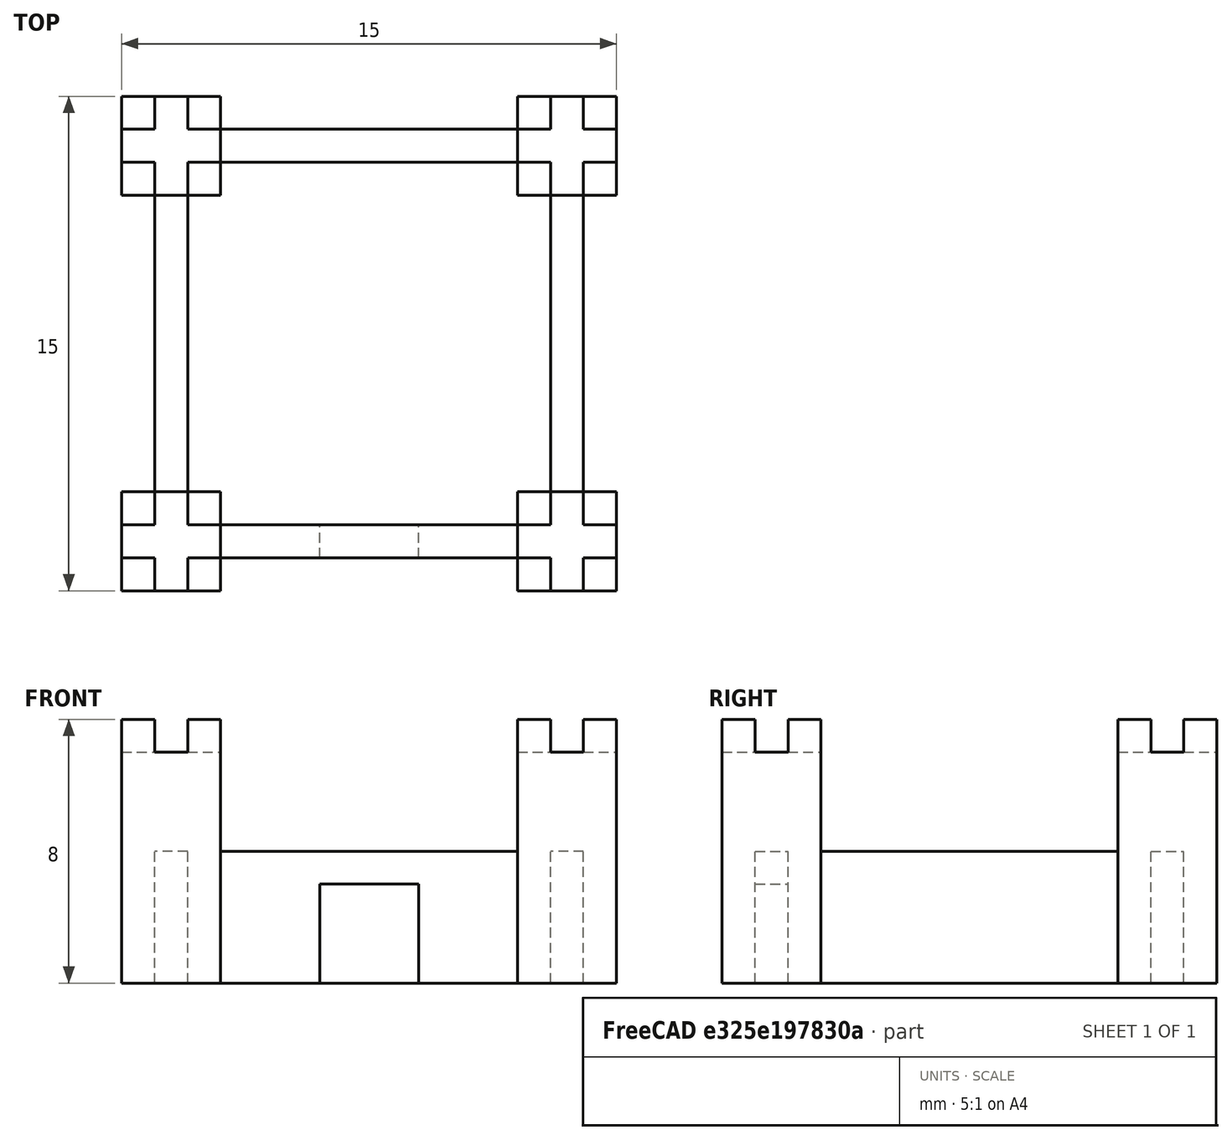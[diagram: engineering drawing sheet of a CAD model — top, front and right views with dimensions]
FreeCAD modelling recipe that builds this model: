
FCSTD DOCUMENT  (FreeCAD 0.20R29177 +233 (Git))
Label: Castillo
License: Creative Commons Attribution-ShareAlike
LicenseURL: http://creativecommons.org/licenses/by-sa/4.0/
objects: Part::Box×25, Part::MultiFuse×23, Part::Cut×1
note: 49 computed .brp shape members not serialized (recipe doc carries the construction recipe); baked Part::Feature solids carry a one-line shape summary decoded from their .brp

FEATURE [Part::Box] Box  label="Cubo"
  AttacherType = Attacher::AttachEngine3D
  Height = 4
  Length = 9
  Width = 1
FEATURE [Part::Box] Box001  label="Cubo001"
  AttacherType = Attacher::AttachEngine3D
  Height = 7
  Length = 3
  Placement = pos=(-3,-1,0) rot=(0,0,1;0rad)
  Width = 3
FEATURE [Part::Box] Box003  label="Cubo003"
  AttacherType = Attacher::AttachEngine3D
  Height = 4
  Length = 9
  Placement = pos=(-1,2,0) rot=(0,0,1;1.5708rad)
  Width = 1
FEATURE [Part::Box] Box004  label="Cubo004"
  AttacherType = Attacher::AttachEngine3D
  Height = 4
  Length = 9
  Placement = pos=(11,2,0) rot=(0,0,1;1.5708rad)
  Width = 1
FEATURE [Part::Box] Box005  label="Cubo005"
  AttacherType = Attacher::AttachEngine3D
  Height = 1
  Length = 1
  Placement = pos=(-1,1,7) rot=(0,0,1;0rad)
  Width = 1
FEATURE [Part::Box] Box006  label="Cubo006"
  AttacherType = Attacher::AttachEngine3D
  Height = 1
  Length = 1
  Placement = pos=(-1,-1,7) rot=(0,0,1;0rad)
  Width = 1
FEATURE [Part::Box] Box007  label="Cubo007"
  AttacherType = Attacher::AttachEngine3D
  Height = 1
  Length = 1
  Placement = pos=(-3,-1,7) rot=(0,0,1;0rad)
  Width = 1
FEATURE [Part::Box] Box008  label="Cubo008"
  AttacherType = Attacher::AttachEngine3D
  Height = 1
  Length = 1
  Placement = pos=(-3,1,7) rot=(0,0,1;0rad)
  Width = 1
FEATURE [Part::MultiFuse] Fusion
  Refine = true
  Shapes = -> [Box001,Box007]
FEATURE [Part::MultiFuse] Fusion001
  Refine = true
  Shapes = -> [Fusion,Box008]
FEATURE [Part::MultiFuse] Fusion002
  Refine = true
  Shapes = -> [Fusion001,Box006]
FEATURE [Part::MultiFuse] Fusion003
  Refine = true
  Shapes = -> [Fusion002,Box005]
FEATURE [Part::Box] Box009  label="Cubo009"
  AttacherType = Attacher::AttachEngine3D
  Height = 7
  Length = 3
  Placement = pos=(-3,-1,0) rot=(0,0,1;0rad)
  Width = 3
FEATURE [Part::Box] Box010  label="Cubo010"
  AttacherType = Attacher::AttachEngine3D
  Height = 1
  Length = 1
  Placement = pos=(-1,1,7) rot=(0,0,1;0rad)
  Width = 1
FEATURE [Part::Box] Box011  label="Cubo011"
  AttacherType = Attacher::AttachEngine3D
  Height = 1
  Length = 1
  Placement = pos=(-1,-1,7) rot=(0,0,1;0rad)
  Width = 1
FEATURE [Part::Box] Box012  label="Cubo012"
  AttacherType = Attacher::AttachEngine3D
  Height = 1
  Length = 1
  Placement = pos=(-3,-1,7) rot=(0,0,1;0rad)
  Width = 1
FEATURE [Part::Box] Box013  label="Cubo013"
  AttacherType = Attacher::AttachEngine3D
  Height = 1
  Length = 1
  Placement = pos=(-3,1,7) rot=(0,0,1;0rad)
  Width = 1
FEATURE [Part::MultiFuse] Fusion004
  Refine = true
  Shapes = -> [Box009,Box012]
FEATURE [Part::MultiFuse] Fusion005
  Refine = true
  Shapes = -> [Fusion004,Box013]
FEATURE [Part::MultiFuse] Fusion006
  Refine = true
  Shapes = -> [Fusion005,Box011]
FEATURE [Part::MultiFuse] Fusion007
  Placement = pos=(12,0,0) rot=(0,0,1;0rad)
  Refine = true
  Shapes = -> [Fusion006,Box010]
FEATURE [Part::Box] Box014  label="Cubo014"
  AttacherType = Attacher::AttachEngine3D
  Height = 7
  Length = 3
  Placement = pos=(-3,-1,0) rot=(0,0,1;0rad)
  Width = 3
FEATURE [Part::Box] Box015  label="Cubo015"
  AttacherType = Attacher::AttachEngine3D
  Height = 1
  Length = 1
  Placement = pos=(-1,1,7) rot=(0,0,1;0rad)
  Width = 1
FEATURE [Part::Box] Box016  label="Cubo016"
  AttacherType = Attacher::AttachEngine3D
  Height = 1
  Length = 1
  Placement = pos=(-1,-1,7) rot=(0,0,1;0rad)
  Width = 1
FEATURE [Part::Box] Box017  label="Cubo017"
  AttacherType = Attacher::AttachEngine3D
  Height = 1
  Length = 1
  Placement = pos=(-3,-1,7) rot=(0,0,1;0rad)
  Width = 1
FEATURE [Part::Box] Box018  label="Cubo018"
  AttacherType = Attacher::AttachEngine3D
  Height = 1
  Length = 1
  Placement = pos=(-3,1,7) rot=(0,0,1;0rad)
  Width = 1
FEATURE [Part::MultiFuse] Fusion008
  Refine = true
  Shapes = -> [Box014,Box017]
FEATURE [Part::MultiFuse] Fusion009
  Refine = true
  Shapes = -> [Fusion008,Box018]
FEATURE [Part::MultiFuse] Fusion010
  Refine = true
  Shapes = -> [Fusion009,Box016]
FEATURE [Part::MultiFuse] Fusion011
  Placement = pos=(12,12,0) rot=(0,0,1;0rad)
  Refine = true
  Shapes = -> [Fusion010,Box015]
FEATURE [Part::Box] Box019  label="Cubo019"
  AttacherType = Attacher::AttachEngine3D
  Height = 7
  Length = 3
  Placement = pos=(-3,-1,0) rot=(0,0,1;0rad)
  Width = 3
FEATURE [Part::Box] Box020  label="Cubo020"
  AttacherType = Attacher::AttachEngine3D
  Height = 1
  Length = 1
  Placement = pos=(-1,1,7) rot=(0,0,1;0rad)
  Width = 1
FEATURE [Part::Box] Box021  label="Cubo021"
  AttacherType = Attacher::AttachEngine3D
  Height = 1
  Length = 1
  Placement = pos=(-1,-1,7) rot=(0,0,1;0rad)
  Width = 1
FEATURE [Part::Box] Box022  label="Cubo022"
  AttacherType = Attacher::AttachEngine3D
  Height = 1
  Length = 1
  Placement = pos=(-3,-1,7) rot=(0,0,1;0rad)
  Width = 1
FEATURE [Part::Box] Box023  label="Cubo023"
  AttacherType = Attacher::AttachEngine3D
  Height = 1
  Length = 1
  Placement = pos=(-3,1,7) rot=(0,0,1;0rad)
  Width = 1
FEATURE [Part::MultiFuse] Fusion012
  Refine = true
  Shapes = -> [Box019,Box022]
FEATURE [Part::MultiFuse] Fusion013
  Refine = true
  Shapes = -> [Fusion012,Box023]
FEATURE [Part::MultiFuse] Fusion014
  Refine = true
  Shapes = -> [Fusion013,Box021]
FEATURE [Part::MultiFuse] Fusion015
  Placement = pos=(0,12,0) rot=(0,0,1;0rad)
  Refine = true
  Shapes = -> [Fusion014,Box020]
FEATURE [Part::Box] Box024  label="Cubo024"
  AttacherType = Attacher::AttachEngine3D
  Height = 4
  Length = 9
  Placement = pos=(0,12,0) rot=(0,0,1;0rad)
  Width = 1
FEATURE [Part::Box] Box025  label="Cubo025"
  AttacherType = Attacher::AttachEngine3D
  Height = 3
  Length = 3
  Placement = pos=(3,0,0) rot=(0,0,1;0rad)
  Width = 1
FEATURE [Part::Cut] Cut
  Base = -> Box
  Refine = true
  Tool = -> Box025
FEATURE [Part::MultiFuse] Fusion016
  Refine = true
  Shapes = -> [Cut,Fusion003]
FEATURE [Part::MultiFuse] Fusion017
  Refine = true
  Shapes = -> [Fusion016,Fusion007]
FEATURE [Part::MultiFuse] Fusion018
  Refine = true
  Shapes = -> [Fusion017,Box004]
FEATURE [Part::MultiFuse] Fusion019
  Refine = true
  Shapes = -> [Fusion018,Box003]
FEATURE [Part::MultiFuse] Fusion020
  Refine = true
  Shapes = -> [Fusion019,Fusion015]
FEATURE [Part::MultiFuse] Fusion021
  Refine = true
  Shapes = -> [Fusion020,Box024]
FEATURE [Part::MultiFuse] Fusion022
  Refine = true
  Shapes = -> [Fusion021,Fusion011]
